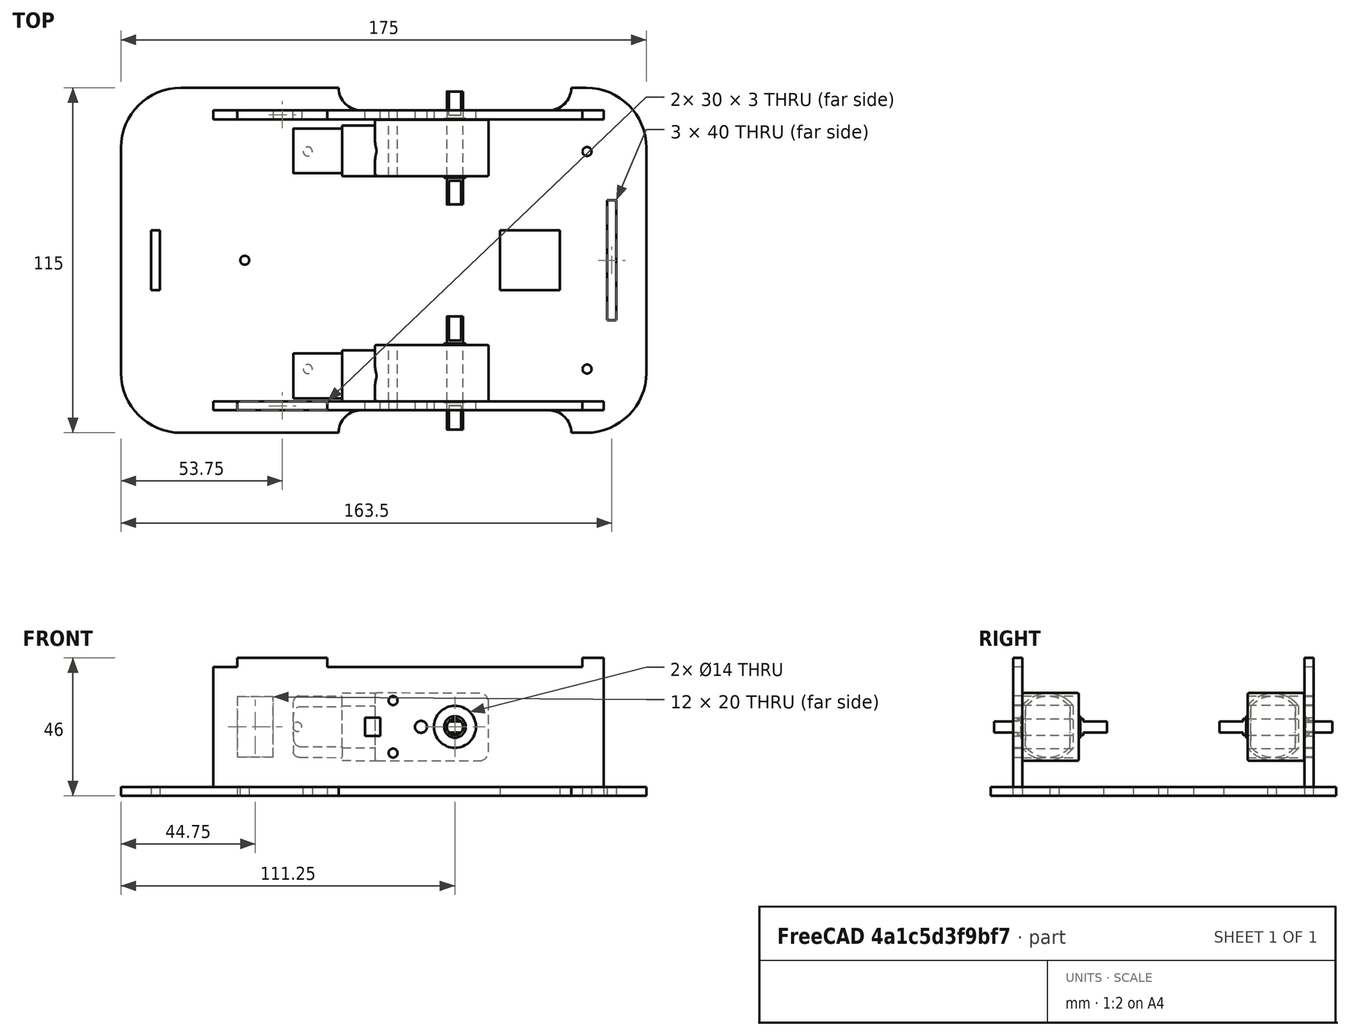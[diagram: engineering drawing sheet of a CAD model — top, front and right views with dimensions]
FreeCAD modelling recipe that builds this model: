
FCSTD DOCUMENT  (FreeCAD 0.15R4671 (Git))
Label: EduRoMAA
License: CreativeCommons Attribution-ShareAlike
LicenseURL: http://creativecommons.org/licenses/by-sa/4.0/
objects: Part::Feature×5, Part::Part2DObjectPython×5
note: 10 computed .brp shape members not serialized (recipe doc carries the construction recipe); baked Part::Feature solids carry a one-line shape summary decoded from their .brp

FEATURE [Part::Feature] Pocket  label="TapaInferior"
  shape: bbox 175 x 115 x 3 mm, 51 faces (baked)
FEATURE [Part::Feature] Pocket001  label="LadoDerecho"
  Placement = pos=(0,-47,0) rot=(1,0,0;1.5708rad)
  shape: bbox 130 x 3 x 46 mm, 26 faces (baked)
FEATURE [Part::Feature] Pocket002  label="LadoIzquierdo"
  Placement = pos=(0,50,0) rot=(1,0,0;1.5708rad)
  shape: bbox 130 x 3 x 46 mm, 31 faces (baked)
FEATURE [Part::Feature] Part__Feature  label="MotorDerecho"
  Placement = pos=(52.5,-56,14.15) rot=(0.519988,-0.519988,-0.677661;1.95044rad)
  shape: bbox 65.28 x 37.6 x 23 mm, 69 faces (baked)
FEATURE [Part::Feature] Part__Feature001  label="MotorIzquierdo"
  Placement = pos=(52.5,19,14.15) rot=(0.519988,-0.519988,-0.677661;1.95044rad)
  shape: bbox 65.28 x 37.6 x 23 mm, 69 faces (baked)
FEATURE [Part::Part2DObjectPython] Shape2DView  label="TapaInferiorShape2DView"  # Draft 2D object (typed FeaturePython)
  Base = -> Pocket
  HiddenLines = false
  Projection = (0,0,1)
  ProjectionMode = 0
  SegmentLength = 0.05
  Tessellation = false
FEATURE [Part::Part2DObjectPython] Shape2DView001  label="LadoDerechoShape2DView"  # Draft 2D object (typed FeaturePython)
  Base = -> Pocket001
  HiddenLines = false
  Projection = (0,0,1)
  ProjectionMode = 0
  SegmentLength = 0.05
  Tessellation = false
FEATURE [Part::Part2DObjectPython] Shape2DView002  label="LadoIzquierdoShape2DView"  # Draft 2D object (typed FeaturePython)
  Base = -> Pocket002
  HiddenLines = false
  Projection = (0,0,1)
  ProjectionMode = 0
  SegmentLength = 0.05
  Tessellation = false
FEATURE [Part::Part2DObjectPython] Shape2DView003  label="MotorDerechoShape2DView"  # Draft 2D object (typed FeaturePython)
  Base = -> Part__Feature
  HiddenLines = false
  Projection = (0,0,1)
  ProjectionMode = 0
  SegmentLength = 0.05
  Tessellation = false
FEATURE [Part::Part2DObjectPython] Shape2DView004  label="MotorIzquierdoShape2DView"  # Draft 2D object (typed FeaturePython)
  Base = -> Part__Feature001
  HiddenLines = false
  Projection = (0,0,1)
  ProjectionMode = 0
  SegmentLength = 0.05
  Tessellation = false
